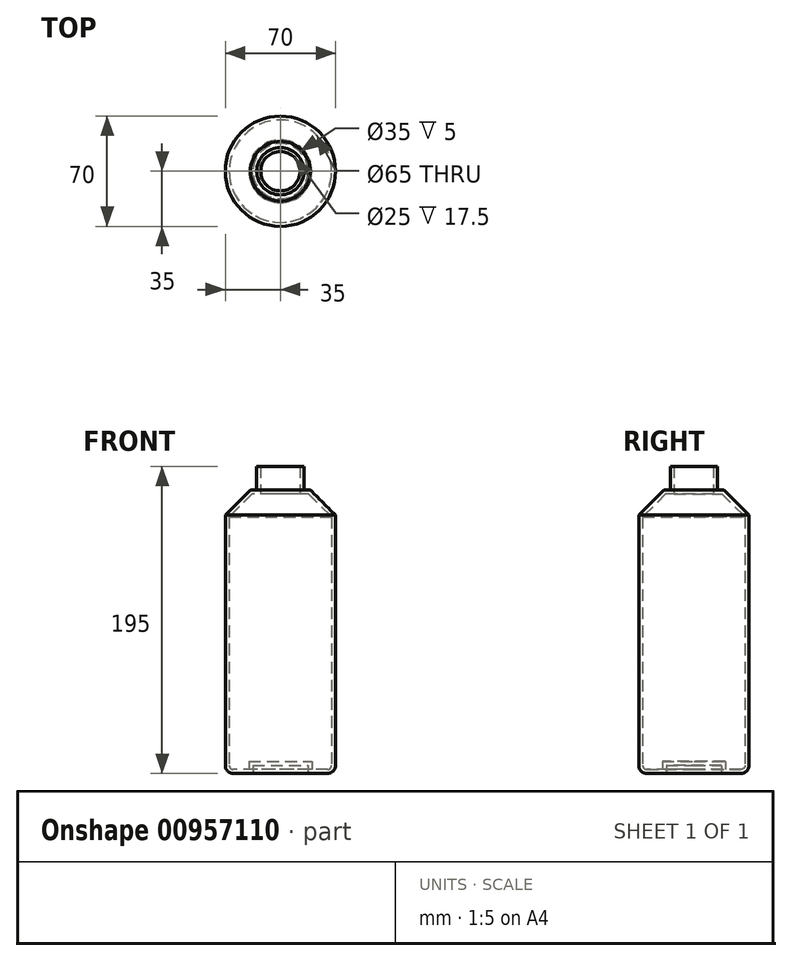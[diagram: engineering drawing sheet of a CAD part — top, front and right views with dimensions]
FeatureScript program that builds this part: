
annotation { "Feature Type Name" : "Feature", "Feature Type Description" : "" }
export const myFeature = defineFeature(function(context is Context, id is Id, definition is map)
    precondition{}
    {
        {
            var Q0;
            Q0=qCreatedBy(makeId("Top.planeOp"),FACE);
            var sketch = newSketch(context, id + "F0", { "sketchPlane" : qUnion([Q0])});
            skCircle(sketch, "E0", {"center": v(0, 0) * mm, "radius": 35 * mm});
            skSolve(sketch);
        }
        {
            var Q0;
            Q0 = qSketchRegion(id + "F0", true);
            extrude(context, id + "F1", {"entities" : qUnion([Q0]), "depth" : 180 * mm, "offsetDistance" : 25 * mm});
        }
        {
            var Q0;
            Q0=makeQuery(id+"F1.opExtrude","CAP_FACE",FACE,{"disambiguationData":[OSD([sQuery(id+"F0.wireOp",EDGE,"E0")])],"isStart":false});
            var sketch = newSketch(context, id + "F2", { "sketchPlane" : qUnion([Q0])});
            skCircle(sketch, "E1", {"center": v(0, 0) * mm, "radius": 15 * mm});
            skSolve(sketch);
        }
        {
            var Q0;
            Q0 = qSketchRegion(id + "F2", true);
            extrude(context, id + "F3", {"entities" : qUnion([Q0]), "operationType" : NewBodyOperationType.ADD, "depth" : 15 * mm, "offsetDistance" : 25 * mm});
        }
        {
            var Q0;
            Q0=makeQuery(id+"F1.opExtrude","CAP_EDGE",EDGE,{"disambiguationData":[OSD([sQuery(id+"F0.wireOp",EDGE,"E0")])],"isStart":true});
            fillet(context, id + "F4", {"entities" : qUnion([Q0]), "radius" : 5 * mm, "tangentPropagation" : true, "allowEdgeOverflow" : false});
        }
        {
            var Q0;
            Q0=makeQuery(id+"F1.opExtrude","CAP_EDGE",EDGE,{"disambiguationData":[OSD([sQuery(id+"F0.wireOp",EDGE,"E0")])],"isStart":false});
            chamfer(context, id + "F5", {"entities" : qUnion([Q0]), "width" : 16 * mm, "tangentPropagation" : true});
        }
        {
            var Q0;
            Q0=makeQuery(id+"F1.opExtrude","CAP_FACE",FACE,{"disambiguationData":[OSD([sQuery(id+"F0.wireOp",EDGE,"E0")])],"isStart":true});
            var sketch = newSketch(context, id + "F6", { "sketchPlane" : qUnion([Q0])});
            skCircle(sketch, "E2", {"center": v(0, 0) * mm, "radius": 17.5 * mm});
            skSolve(sketch);
        }
        {
            var Q0;
            Q0 = qSketchRegion(id + "F6", true);
            extrude(context, id + "F7", {"entities" : qUnion([Q0]), "operationType" : NewBodyOperationType.REMOVE, "oppositeDirection" : true, "depth" : 5 * mm, "offsetDistance" : 25 * mm});
        }
        {
            var Q0;
            Q0=makeQuery(id+"F3.opExtrude","CAP_FACE",FACE,{"disambiguationData":[OSD([sQuery(id+"F2.wireOp",EDGE,"E1")])],"isStart":false});
            shell(context, id + "F8", {"entities" : qUnion([Q0]), "thickness" : 2.5 * mm});
        }
    });
